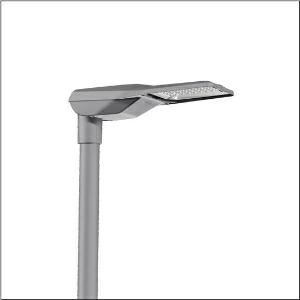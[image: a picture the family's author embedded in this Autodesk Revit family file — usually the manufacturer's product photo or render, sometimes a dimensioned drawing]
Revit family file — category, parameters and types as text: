
# Revit family: streetlight_sl_21_iq_mini___p1_0a_5xe2a31d08hb_09ea
name_source: partatom
category: Lighting Fixtures
units: mm (PartAtom-declared; Revit-internal decimal feet)

## family parameters
Cut with Voids When Loaded = No
Host = Face
Light Source = No
Part Type = Normal
Room Calculation Point = No
Round Connector Dimension = Use Diameter
Shared = No

## types (1)
- --- (1 x LED, 9450 lm, 70.9 W, 3000K)
    Apparent Load = 71 VA
    CIE Flux Codes = 21 50 90 100 100
    Color Rendering = 70
    Color Temperature = 3000K
    Default Elevation = 1800 mm
    Description = Streetlight SL 21 iQ mini, mast luminaire, primary light control with lens, of PMMA, primary optical cover: cover, of toughened safety glass, transparent, light distribution: P1.0a, light emission: direct distribution, primary light characteristic: asymmetric, installation type: post-top, side-entry, LED, High Power LED, rated luminous flux: 9.450lm, luminous efficacy: 133lm/W, light colour: 730, colour temperature: 3000K, control: Auto-Match, Temp-Guard, Lumen-Switch, Night-Set, Smart-Wire, Light-Fading, Desk-Remote (wireless, voltage-free reading and setting of iQ features in the workshop via application-optimized NFC function/RFID function), optimised constant luminous flux control (CLO 2.0), presetting dimming linear, mains connection: 220..240V, AC, 50/60Hz, start of lifetime: 71W, end of service life: 75W, reduction: 31W, luminaire housing, of diecast aluminium, powder-coated, Siteco® metallic grey (DB 702S), corrosivity category C5 mid according to DIN EN ISO 12944, please order mast flange separately, inclination adjustable: 0°, 5°, 10°, 15°, sealing non-destructively replaceable, multi-level sealing system, length: 628mm, width: 235mm, height: 110mm, mast flange for spigot size: 42mm (side-entry): 5XC10008XM4, 60/48mm (side-entry/post-top): 5XC10108XM2, 76/60mm (side-entry/post-top): 5XC10108XM1, protection rating (complete): IP66, insulation class (complete): insulation class II (safety insulation), certification: CE, ENEC, ENEC+, VDE, impact resistance: IK09, permissible operating ambient temperature for outdoor applications: -40..+50°C, standard-compliant lighting for roads and squares, packaging unit: 1 piece

Light Distribution: P1.0a
    Height = 110 mm
    Lamp = 1 x LED
    Lamp Light Flux = 9450 lm
    Lamp Power = 70.9 W
    Lamp count = 1
    Length = 625 mm
    Luminous efficacy = 133 lm/W
    Manufacturer = Siteco
    ModVariant = No
    Model = 5XE2A31D08HB
    Number of Poles = 1
    OnlyDefault = Yes
    Power Factor = 1
    Product Name = Streetlight SL 21 iQ mini | P1.0a
    Product group = mast luminaire | pylon top
    ProductGroupID = 6100
    Protection Class = Protection class II
    Protection Degree = IP 66
    RLX_Detail_Level = 1
    RLX_Emergency_Light_Flux = 0 lm
    RLX_Emergency_Type = 0
    RLX_Emergency_Type_DB = No
    RlxData = <blob elided: 103609 chars, md5=7ad84c09>
    Socket = socket
    Standby Power = 0 W
    System Light Flux = 9450 lm
    System Power = 71 W
    Type Comments = factory setting: luminous flux: 100 % | dim-lin: 254 | 711 mA
    Type Image = l_1003519.jpg
    URL = http://relux.com
    VarID = @adj_090039
    Voltage = 0 V
    Weight = 0.00 kg
    Width = 234 mm

## geometry (parser evidence)
native form markers: Blend x4, Sweep x12
no freeform markers — native parametric forms only
